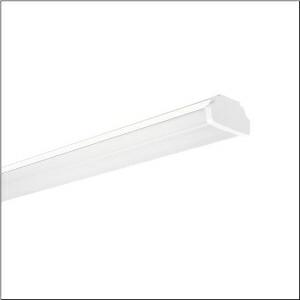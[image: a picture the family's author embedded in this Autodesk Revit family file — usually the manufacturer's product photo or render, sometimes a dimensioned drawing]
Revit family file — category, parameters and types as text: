
# Revit family: modario_r__31_gen_2_53bm812mv4fxd2_4edd
name_source: partatom
category: Lighting Fixtures
units: mm (PartAtom-declared; Revit-internal decimal feet)

## family parameters
Cut with Voids When Loaded = No
Host = Face
Light Source = No
Part Type = Normal
Room Calculation Point = No
Round Connector Dimension = Use Diameter
Shared = No

## types (1)
- --- (1 x LED, 15440 lm, 82.3 W, 4000K)
    Apparent Load = 82 VA
    CIE Flux Codes = 47 80 95 93 100
    Color Rendering = 80
    Color Temperature = 4000K
    Default Elevation = 1800 mm
    Description = Modario® 31 Gen.2, luminaire insert, of sheet steel, coil coated, white, length: 1.495mm, width: 81mm, height: 82mm, 5x system unit, system units: 299mm, LED rated luminous flux: 15.440lm, light colour: 840, control gear: ON/OFF Multilumen, control gear: ECG, with plug, 3-pole, with phase selection, mains connection: 220..240V, AC, 50/60Hz, rated input power: 82W, through-wiring accessed according to module size, primary optical cover: cover, of PMMA, light emission: direct distribution, primary light characteristic: symmetric, protection rating (complete): IP20, protection rating (LED compartment): IP50, insulation class (complete): insulation class I (protective earthing), certification: CE, ENEC, VDE, UKCA, impact resistance: IK03, permissible ambient temperature for indoor applications: -35..+35°C, corresponds to IFS (International Featured Standards) requirements for safety and quality in the food industry, reducing of maximum allowable ambient temperature of 5°C with ceiling mounting, IP40 when using the optional accessory 5TP9018, packaging unit: 1 piece
    Height = 92 mm
    Lamp = 1 x LED
    Lamp Light Flux = 15440 lm
    Lamp Power = 82.3 W
    Lamp count = 1
    Length = 1495 mm
    Luminous efficacy = 188 lm/W
    Manufacturer = Siteco
    ModVariant = No
    Model = 53BM812MV4FXD2
    Mounting Place = Ceiling
    Mounting Type = Pendant
    Number of Poles = 1
    OnlyDefault = Yes
    Power Factor = 1
    Product Name = Modario® 31 Gen.2
    Product group = luminaire insert
    ProductGroupID = 902
    Protection Class = Protection class I
    Protection Degree = IP 20
    RLX_Detail_Level = 1
    RLX_Emergency_Light_Flux = 0 lm
    RLX_Emergency_Type = 0
    RLX_Emergency_Type_DB = No
    RlxData = <blob elided: 40085 chars, md5=d08271a0>
    Socket = socket
    Standby Power = 0 W
    System Light Flux = 15440 lm
    System Power = 82 W
    Type Comments = factory setting: luminous flux: 100 % | (A | C | E) | 193 mA
    Type Image = l_1341886.jpg
    URL = http://relux.com
    VarID = @adj_043390
    Voltage = 0 V
    Weight = 0.00 kg
    Width = 81 mm

## geometry (parser evidence)
native form markers: Blend x4, Sweep x12
no freeform markers — native parametric forms only
